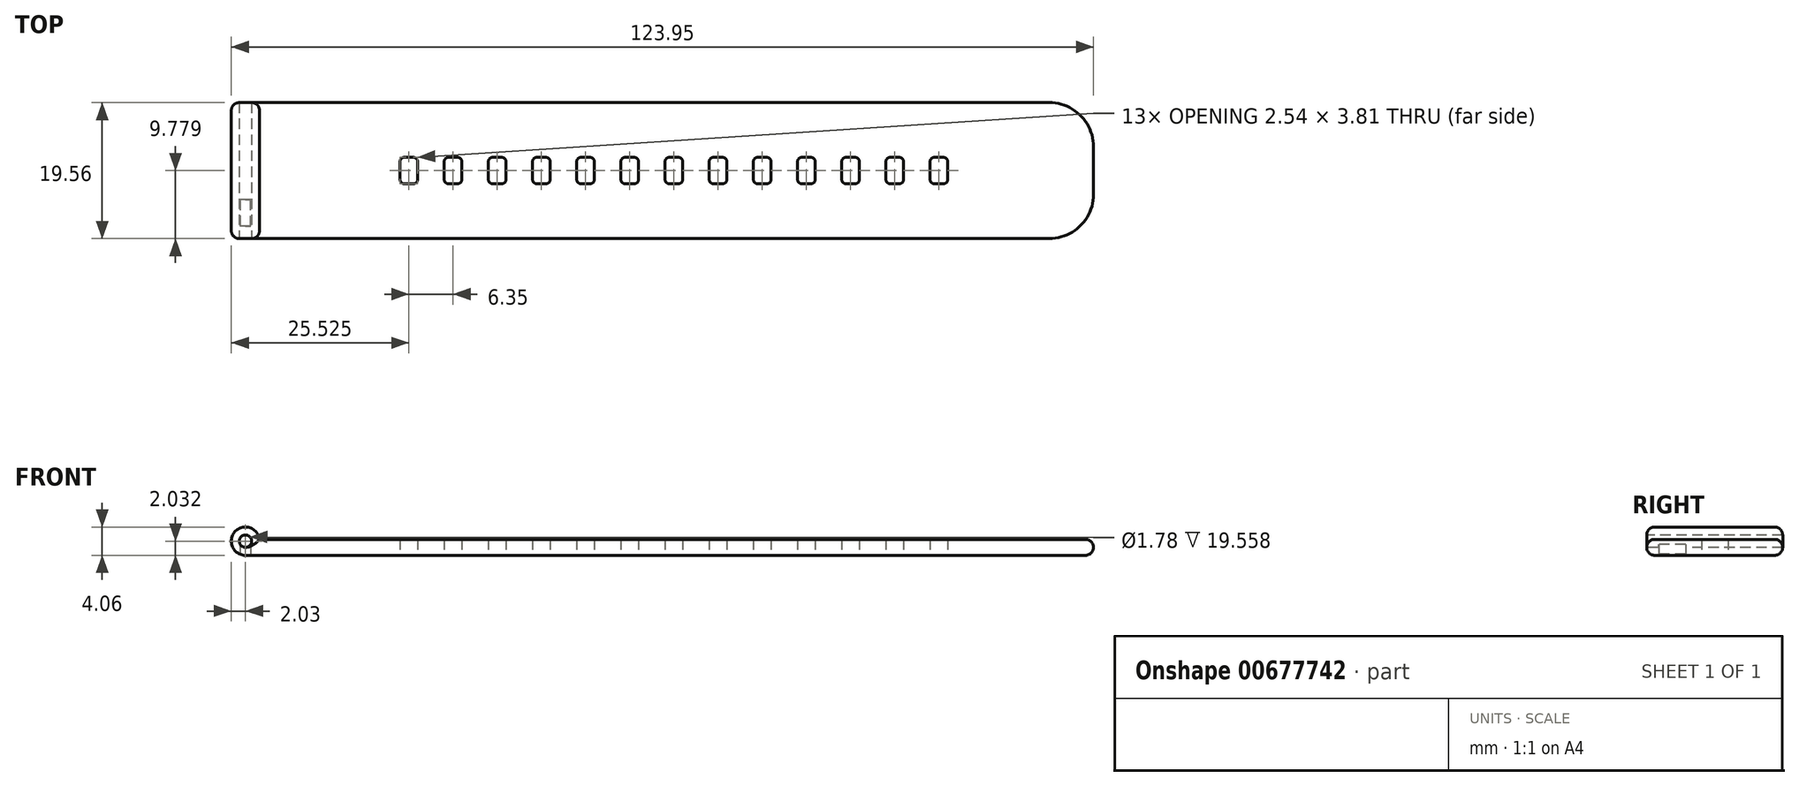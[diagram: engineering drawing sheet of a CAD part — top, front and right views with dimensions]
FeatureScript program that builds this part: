
annotation { "Feature Type Name" : "Feature", "Feature Type Description" : "" }
export const myFeature = defineFeature(function(context is Context, id is Id, definition is map)
    precondition{}
    {
        {
            var Q0;
            Q0=qCreatedBy(makeId("Top.planeOp"),FACE);
            var sketch = newSketch(context, id + "F0", { "sketchPlane" : qUnion([Q0])});
            skLineSegment(sketch, "E0.bottom", {"start": v(0, 0) * mm, "end": v(115.57, 0) * mm});
            skLineSegment(sketch, "E0.top", {"start": v(0, 19.56) * mm, "end": v(115.57, 19.56) * mm});
            skLineSegment(sketch, "E0.left", {"start": v(0, 0) * mm, "end": v(0, 19.56) * mm});
            skLineSegment(sketch, "E0.right", {"start": v(121.92, 6.35) * mm, "end": v(121.92, 13.2) * mm});
            skPoint(sketch, "E1.visualSharp", {"position": v(121.92, 19.56) * mm});
            skArc(sketch, "E1.filletArc", {"start": v(121.92, 13.2) * mm, "mid": v(120.06, 17.7) * mm, "end": v(115.57, 19.56) * mm});
            skPoint(sketch, "E2.visualSharp", {"position": v(121.92, 0) * mm});
            skArc(sketch, "E2.filletArc", {"start": v(115.57, 0) * mm, "mid": v(120.06, 1.86) * mm, "end": v(121.92, 6.35) * mm});
            skLineSegment(sketch, "E3.bottom", {"start": v(24.13, 7.87) * mm, "end": v(22.86, 7.87) * mm});
            skLineSegment(sketch, "E3.top", {"start": v(24.13, 11.68) * mm, "end": v(22.86, 11.68) * mm});
            skLineSegment(sketch, "E3.left", {"start": v(24.77, 8.5) * mm, "end": v(24.77, 11.05) * mm});
            skLineSegment(sketch, "E3.right", {"start": v(22.23, 8.5) * mm, "end": v(22.23, 11.05) * mm});
            skPoint(sketch, "E3.middle", {"position": v(23.5, 9.78) * mm});
            skPoint(sketch, "E3.middle.positionSnap0", {"position": v(0, 9.78) * mm});
            skPoint(sketch, "E3.centerSnap0", {"position": v(0, 9.78) * mm});
            skPoint(sketch, "E4.visualSharp", {"position": v(22.23, 11.68) * mm});
            skArc(sketch, "E4.filletArc", {"start": v(22.86, 11.68) * mm, "mid": v(22.41, 11.5) * mm, "end": v(22.22, 11.05) * mm});
            skPoint(sketch, "E5.visualSharp", {"position": v(24.77, 11.68) * mm});
            skArc(sketch, "E5.filletArc", {"start": v(24.77, 11.05) * mm, "mid": v(24.58, 11.5) * mm, "end": v(24.13, 11.68) * mm});
            skPoint(sketch, "E6.visualSharp", {"position": v(24.77, 7.87) * mm});
            skArc(sketch, "E6.filletArc", {"start": v(24.13, 7.87) * mm, "mid": v(24.58, 8.06) * mm, "end": v(24.77, 8.5) * mm});
            skPoint(sketch, "E7.visualSharp", {"position": v(22.23, 7.87) * mm});
            skArc(sketch, "E7.filletArc", {"start": v(22.23, 8.5) * mm, "mid": v(22.41, 8.06) * mm, "end": v(22.86, 7.87) * mm});
            skPoint(sketch, "E8.1.0.0", {"position": v(28.58, 7.87) * mm});
            skPoint(sketch, "E8.1.0.1", {"position": v(31.12, 7.87) * mm});
            skPoint(sketch, "E8.1.0.2", {"position": v(28.58, 11.68) * mm});
            skPoint(sketch, "E8.1.0.3", {"position": v(31.12, 11.68) * mm});
            skPoint(sketch, "E8.1.0.4", {"position": v(29.85, 9.78) * mm});
            skLineSegment(sketch, "E8.1.0.5", {"start": v(30.48, 11.68) * mm, "end": v(29.21, 11.68) * mm});
            skLineSegment(sketch, "E8.1.0.6", {"start": v(31.12, 8.5) * mm, "end": v(31.12, 11.05) * mm});
            skLineSegment(sketch, "E8.1.0.7", {"start": v(28.58, 8.5) * mm, "end": v(28.58, 11.05) * mm});
            skArc(sketch, "E8.1.0.8", {"start": v(31.12, 11.05) * mm, "mid": v(30.93, 11.5) * mm, "end": v(30.48, 11.68) * mm});
            skArc(sketch, "E8.1.0.9", {"start": v(29.21, 11.68) * mm, "mid": v(28.76, 11.5) * mm, "end": v(28.57, 11.05) * mm});
            skArc(sketch, "E8.1.0.10", {"start": v(30.48, 7.87) * mm, "mid": v(30.93, 8.06) * mm, "end": v(31.12, 8.5) * mm});
            skLineSegment(sketch, "E8.1.0.11", {"start": v(30.48, 7.87) * mm, "end": v(29.21, 7.87) * mm});
            skArc(sketch, "E8.1.0.12", {"start": v(28.58, 8.5) * mm, "mid": v(28.76, 8.06) * mm, "end": v(29.21, 7.87) * mm});
            skPoint(sketch, "E8.2.0.0", {"position": v(34.93, 7.87) * mm});
            skPoint(sketch, "E8.2.0.1", {"position": v(37.47, 7.87) * mm});
            skPoint(sketch, "E8.2.0.2", {"position": v(34.93, 11.68) * mm});
            skPoint(sketch, "E8.2.0.3", {"position": v(37.47, 11.68) * mm});
            skPoint(sketch, "E8.2.0.4", {"position": v(36.2, 9.78) * mm});
            skLineSegment(sketch, "E8.2.0.5", {"start": v(36.83, 11.68) * mm, "end": v(35.56, 11.68) * mm});
            skLineSegment(sketch, "E8.2.0.6", {"start": v(37.47, 8.5) * mm, "end": v(37.47, 11.05) * mm});
            skLineSegment(sketch, "E8.2.0.7", {"start": v(34.93, 8.5) * mm, "end": v(34.93, 11.05) * mm});
            skArc(sketch, "E8.2.0.8", {"start": v(37.46, 11.05) * mm, "mid": v(37.28, 11.5) * mm, "end": v(36.83, 11.68) * mm});
            skArc(sketch, "E8.2.0.9", {"start": v(35.56, 11.68) * mm, "mid": v(35.11, 11.5) * mm, "end": v(34.92, 11.05) * mm});
            skArc(sketch, "E8.2.0.10", {"start": v(36.83, 7.87) * mm, "mid": v(37.28, 8.06) * mm, "end": v(37.47, 8.5) * mm});
            skLineSegment(sketch, "E8.2.0.11", {"start": v(36.83, 7.87) * mm, "end": v(35.56, 7.87) * mm});
            skArc(sketch, "E8.2.0.12", {"start": v(34.93, 8.5) * mm, "mid": v(35.11, 8.06) * mm, "end": v(35.56, 7.87) * mm});
            skPoint(sketch, "E8.3.0.0", {"position": v(41.28, 7.87) * mm});
            skPoint(sketch, "E8.3.0.1", {"position": v(43.82, 7.87) * mm});
            skPoint(sketch, "E8.3.0.2", {"position": v(41.28, 11.68) * mm});
            skPoint(sketch, "E8.3.0.3", {"position": v(43.82, 11.68) * mm});
            skPoint(sketch, "E8.3.0.4", {"position": v(42.55, 9.78) * mm});
            skLineSegment(sketch, "E8.3.0.5", {"start": v(43.18, 11.68) * mm, "end": v(41.91, 11.68) * mm});
            skLineSegment(sketch, "E8.3.0.6", {"start": v(43.82, 8.5) * mm, "end": v(43.82, 11.05) * mm});
            skLineSegment(sketch, "E8.3.0.7", {"start": v(41.28, 8.5) * mm, "end": v(41.28, 11.05) * mm});
            skArc(sketch, "E8.3.0.8", {"start": v(43.82, 11.05) * mm, "mid": v(43.63, 11.5) * mm, "end": v(43.18, 11.68) * mm});
            skArc(sketch, "E8.3.0.9", {"start": v(41.91, 11.68) * mm, "mid": v(41.46, 11.5) * mm, "end": v(41.28, 11.05) * mm});
            skArc(sketch, "E8.3.0.10", {"start": v(43.18, 7.87) * mm, "mid": v(43.63, 8.06) * mm, "end": v(43.82, 8.5) * mm});
            skLineSegment(sketch, "E8.3.0.11", {"start": v(43.18, 7.87) * mm, "end": v(41.91, 7.87) * mm});
            skArc(sketch, "E8.3.0.12", {"start": v(41.28, 8.5) * mm, "mid": v(41.46, 8.06) * mm, "end": v(41.91, 7.87) * mm});
            skPoint(sketch, "E8.4.0.0", {"position": v(47.63, 7.87) * mm});
            skPoint(sketch, "E8.4.0.1", {"position": v(50.17, 7.87) * mm});
            skPoint(sketch, "E8.4.0.2", {"position": v(47.63, 11.68) * mm});
            skPoint(sketch, "E8.4.0.3", {"position": v(50.17, 11.68) * mm});
            skPoint(sketch, "E8.4.0.4", {"position": v(48.9, 9.78) * mm});
            skLineSegment(sketch, "E8.4.0.5", {"start": v(49.53, 11.68) * mm, "end": v(48.26, 11.68) * mm});
            skLineSegment(sketch, "E8.4.0.6", {"start": v(50.17, 8.5) * mm, "end": v(50.17, 11.05) * mm});
            skLineSegment(sketch, "E8.4.0.7", {"start": v(47.63, 8.5) * mm, "end": v(47.63, 11.05) * mm});
            skArc(sketch, "E8.4.0.8", {"start": v(50.16, 11.05) * mm, "mid": v(49.98, 11.5) * mm, "end": v(49.53, 11.68) * mm});
            skArc(sketch, "E8.4.0.9", {"start": v(48.26, 11.68) * mm, "mid": v(47.81, 11.5) * mm, "end": v(47.62, 11.05) * mm});
            skArc(sketch, "E8.4.0.10", {"start": v(49.53, 7.87) * mm, "mid": v(49.98, 8.06) * mm, "end": v(50.17, 8.5) * mm});
            skLineSegment(sketch, "E8.4.0.11", {"start": v(49.53, 7.87) * mm, "end": v(48.26, 7.87) * mm});
            skArc(sketch, "E8.4.0.12", {"start": v(47.63, 8.5) * mm, "mid": v(47.81, 8.06) * mm, "end": v(48.26, 7.87) * mm});
            skPoint(sketch, "E8.5.0.0", {"position": v(53.98, 7.87) * mm});
            skPoint(sketch, "E8.5.0.1", {"position": v(56.52, 7.87) * mm});
            skPoint(sketch, "E8.5.0.2", {"position": v(53.98, 11.68) * mm});
            skPoint(sketch, "E8.5.0.3", {"position": v(56.52, 11.68) * mm});
            skPoint(sketch, "E8.5.0.4", {"position": v(55.25, 9.78) * mm});
            skLineSegment(sketch, "E8.5.0.5", {"start": v(55.88, 11.68) * mm, "end": v(54.61, 11.68) * mm});
            skLineSegment(sketch, "E8.5.0.6", {"start": v(56.52, 8.5) * mm, "end": v(56.52, 11.05) * mm});
            skLineSegment(sketch, "E8.5.0.7", {"start": v(53.98, 8.5) * mm, "end": v(53.98, 11.05) * mm});
            skArc(sketch, "E8.5.0.8", {"start": v(56.52, 11.05) * mm, "mid": v(56.33, 11.5) * mm, "end": v(55.88, 11.68) * mm});
            skArc(sketch, "E8.5.0.9", {"start": v(54.61, 11.68) * mm, "mid": v(54.16, 11.5) * mm, "end": v(53.98, 11.05) * mm});
            skArc(sketch, "E8.5.0.10", {"start": v(55.88, 7.87) * mm, "mid": v(56.33, 8.06) * mm, "end": v(56.52, 8.5) * mm});
            skLineSegment(sketch, "E8.5.0.11", {"start": v(55.88, 7.87) * mm, "end": v(54.61, 7.87) * mm});
            skArc(sketch, "E8.5.0.12", {"start": v(53.98, 8.5) * mm, "mid": v(54.16, 8.06) * mm, "end": v(54.61, 7.87) * mm});
            skPoint(sketch, "E8.6.0.0", {"position": v(60.33, 7.87) * mm});
            skPoint(sketch, "E8.6.0.1", {"position": v(62.87, 7.87) * mm});
            skPoint(sketch, "E8.6.0.2", {"position": v(60.33, 11.68) * mm});
            skPoint(sketch, "E8.6.0.3", {"position": v(62.87, 11.68) * mm});
            skPoint(sketch, "E8.6.0.4", {"position": v(61.6, 9.78) * mm});
            skLineSegment(sketch, "E8.6.0.5", {"start": v(62.23, 11.68) * mm, "end": v(60.96, 11.68) * mm});
            skLineSegment(sketch, "E8.6.0.6", {"start": v(62.87, 8.5) * mm, "end": v(62.87, 11.05) * mm});
            skLineSegment(sketch, "E8.6.0.7", {"start": v(60.33, 8.5) * mm, "end": v(60.33, 11.05) * mm});
            skArc(sketch, "E8.6.0.8", {"start": v(62.87, 11.05) * mm, "mid": v(62.68, 11.5) * mm, "end": v(62.23, 11.68) * mm});
            skArc(sketch, "E8.6.0.9", {"start": v(60.96, 11.68) * mm, "mid": v(60.51, 11.5) * mm, "end": v(60.33, 11.05) * mm});
            skArc(sketch, "E8.6.0.10", {"start": v(62.23, 7.87) * mm, "mid": v(62.68, 8.06) * mm, "end": v(62.87, 8.5) * mm});
            skLineSegment(sketch, "E8.6.0.11", {"start": v(62.23, 7.87) * mm, "end": v(60.96, 7.87) * mm});
            skArc(sketch, "E8.6.0.12", {"start": v(60.33, 8.5) * mm, "mid": v(60.51, 8.06) * mm, "end": v(60.96, 7.87) * mm});
            skPoint(sketch, "E8.7.0.0", {"position": v(66.68, 7.87) * mm});
            skPoint(sketch, "E8.7.0.1", {"position": v(69.22, 7.87) * mm});
            skPoint(sketch, "E8.7.0.2", {"position": v(66.68, 11.68) * mm});
            skPoint(sketch, "E8.7.0.3", {"position": v(69.22, 11.68) * mm});
            skPoint(sketch, "E8.7.0.4", {"position": v(67.95, 9.78) * mm});
            skLineSegment(sketch, "E8.7.0.5", {"start": v(68.58, 11.68) * mm, "end": v(67.31, 11.68) * mm});
            skLineSegment(sketch, "E8.7.0.6", {"start": v(69.22, 8.5) * mm, "end": v(69.22, 11.05) * mm});
            skLineSegment(sketch, "E8.7.0.7", {"start": v(66.68, 8.5) * mm, "end": v(66.68, 11.05) * mm});
            skArc(sketch, "E8.7.0.8", {"start": v(69.22, 11.05) * mm, "mid": v(69.03, 11.5) * mm, "end": v(68.58, 11.68) * mm});
            skArc(sketch, "E8.7.0.9", {"start": v(67.31, 11.68) * mm, "mid": v(66.86, 11.5) * mm, "end": v(66.68, 11.05) * mm});
            skArc(sketch, "E8.7.0.10", {"start": v(68.58, 7.87) * mm, "mid": v(69.03, 8.06) * mm, "end": v(69.22, 8.5) * mm});
            skLineSegment(sketch, "E8.7.0.11", {"start": v(68.58, 7.87) * mm, "end": v(67.31, 7.87) * mm});
            skArc(sketch, "E8.7.0.12", {"start": v(66.68, 8.5) * mm, "mid": v(66.86, 8.06) * mm, "end": v(67.31, 7.87) * mm});
            skPoint(sketch, "E8.8.0.0", {"position": v(73.03, 7.87) * mm});
            skPoint(sketch, "E8.8.0.1", {"position": v(75.57, 7.87) * mm});
            skPoint(sketch, "E8.8.0.2", {"position": v(73.03, 11.68) * mm});
            skPoint(sketch, "E8.8.0.3", {"position": v(75.57, 11.68) * mm});
            skPoint(sketch, "E8.8.0.4", {"position": v(74.3, 9.78) * mm});
            skLineSegment(sketch, "E8.8.0.5", {"start": v(74.93, 11.68) * mm, "end": v(73.66, 11.68) * mm});
            skLineSegment(sketch, "E8.8.0.6", {"start": v(75.57, 8.5) * mm, "end": v(75.57, 11.05) * mm});
            skLineSegment(sketch, "E8.8.0.7", {"start": v(73.03, 8.5) * mm, "end": v(73.03, 11.05) * mm});
            skArc(sketch, "E8.8.0.8", {"start": v(75.57, 11.05) * mm, "mid": v(75.38, 11.5) * mm, "end": v(74.93, 11.68) * mm});
            skArc(sketch, "E8.8.0.9", {"start": v(73.66, 11.68) * mm, "mid": v(73.21, 11.5) * mm, "end": v(73.03, 11.05) * mm});
            skArc(sketch, "E8.8.0.10", {"start": v(74.93, 7.87) * mm, "mid": v(75.38, 8.06) * mm, "end": v(75.57, 8.5) * mm});
            skLineSegment(sketch, "E8.8.0.11", {"start": v(74.93, 7.87) * mm, "end": v(73.66, 7.87) * mm});
            skArc(sketch, "E8.8.0.12", {"start": v(73.03, 8.5) * mm, "mid": v(73.21, 8.06) * mm, "end": v(73.66, 7.87) * mm});
            skPoint(sketch, "E8.9.0.0", {"position": v(79.38, 7.87) * mm});
            skPoint(sketch, "E8.9.0.1", {"position": v(81.92, 7.87) * mm});
            skPoint(sketch, "E8.9.0.2", {"position": v(79.38, 11.68) * mm});
            skPoint(sketch, "E8.9.0.3", {"position": v(81.92, 11.68) * mm});
            skPoint(sketch, "E8.9.0.4", {"position": v(80.65, 9.78) * mm});
            skLineSegment(sketch, "E8.9.0.5", {"start": v(81.28, 11.68) * mm, "end": v(80.01, 11.68) * mm});
            skLineSegment(sketch, "E8.9.0.6", {"start": v(81.92, 8.5) * mm, "end": v(81.92, 11.05) * mm});
            skLineSegment(sketch, "E8.9.0.7", {"start": v(79.38, 8.5) * mm, "end": v(79.38, 11.05) * mm});
            skArc(sketch, "E8.9.0.8", {"start": v(81.92, 11.05) * mm, "mid": v(81.73, 11.5) * mm, "end": v(81.28, 11.68) * mm});
            skArc(sketch, "E8.9.0.9", {"start": v(80.01, 11.68) * mm, "mid": v(79.56, 11.5) * mm, "end": v(79.38, 11.05) * mm});
            skArc(sketch, "E8.9.0.10", {"start": v(81.28, 7.87) * mm, "mid": v(81.73, 8.06) * mm, "end": v(81.92, 8.5) * mm});
            skLineSegment(sketch, "E8.9.0.11", {"start": v(81.28, 7.87) * mm, "end": v(80.01, 7.87) * mm});
            skArc(sketch, "E8.9.0.12", {"start": v(79.38, 8.5) * mm, "mid": v(79.56, 8.06) * mm, "end": v(80.01, 7.87) * mm});
            skPoint(sketch, "E8.10.0.0", {"position": v(85.73, 7.87) * mm});
            skPoint(sketch, "E8.10.0.1", {"position": v(88.27, 7.87) * mm});
            skPoint(sketch, "E8.10.0.2", {"position": v(85.73, 11.68) * mm});
            skPoint(sketch, "E8.10.0.3", {"position": v(88.27, 11.68) * mm});
            skPoint(sketch, "E8.10.0.4", {"position": v(87, 9.78) * mm});
            skLineSegment(sketch, "E8.10.0.5", {"start": v(87.63, 11.68) * mm, "end": v(86.36, 11.68) * mm});
            skLineSegment(sketch, "E8.10.0.6", {"start": v(88.27, 8.5) * mm, "end": v(88.27, 11.05) * mm});
            skLineSegment(sketch, "E8.10.0.7", {"start": v(85.73, 8.5) * mm, "end": v(85.73, 11.05) * mm});
            skArc(sketch, "E8.10.0.8", {"start": v(88.27, 11.05) * mm, "mid": v(88.08, 11.5) * mm, "end": v(87.63, 11.68) * mm});
            skArc(sketch, "E8.10.0.9", {"start": v(86.36, 11.68) * mm, "mid": v(85.91, 11.5) * mm, "end": v(85.73, 11.05) * mm});
            skArc(sketch, "E8.10.0.10", {"start": v(87.63, 7.87) * mm, "mid": v(88.08, 8.06) * mm, "end": v(88.27, 8.5) * mm});
            skLineSegment(sketch, "E8.10.0.11", {"start": v(87.63, 7.87) * mm, "end": v(86.36, 7.87) * mm});
            skArc(sketch, "E8.10.0.12", {"start": v(85.73, 8.5) * mm, "mid": v(85.91, 8.06) * mm, "end": v(86.36, 7.87) * mm});
            skPoint(sketch, "E8.11.0.0", {"position": v(92.08, 7.87) * mm});
            skPoint(sketch, "E8.11.0.1", {"position": v(94.62, 7.87) * mm});
            skPoint(sketch, "E8.11.0.2", {"position": v(92.08, 11.68) * mm});
            skPoint(sketch, "E8.11.0.3", {"position": v(94.62, 11.68) * mm});
            skPoint(sketch, "E8.11.0.4", {"position": v(93.35, 9.78) * mm});
            skLineSegment(sketch, "E8.11.0.5", {"start": v(93.98, 11.68) * mm, "end": v(92.71, 11.68) * mm});
            skLineSegment(sketch, "E8.11.0.6", {"start": v(94.62, 8.5) * mm, "end": v(94.62, 11.05) * mm});
            skLineSegment(sketch, "E8.11.0.7", {"start": v(92.08, 8.5) * mm, "end": v(92.08, 11.05) * mm});
            skArc(sketch, "E8.11.0.8", {"start": v(94.62, 11.05) * mm, "mid": v(94.43, 11.5) * mm, "end": v(93.98, 11.68) * mm});
            skArc(sketch, "E8.11.0.9", {"start": v(92.71, 11.68) * mm, "mid": v(92.26, 11.5) * mm, "end": v(92.08, 11.05) * mm});
            skArc(sketch, "E8.11.0.10", {"start": v(93.98, 7.87) * mm, "mid": v(94.43, 8.06) * mm, "end": v(94.62, 8.5) * mm});
            skLineSegment(sketch, "E8.11.0.11", {"start": v(93.98, 7.87) * mm, "end": v(92.71, 7.87) * mm});
            skArc(sketch, "E8.11.0.12", {"start": v(92.08, 8.5) * mm, "mid": v(92.26, 8.06) * mm, "end": v(92.71, 7.87) * mm});
            skPoint(sketch, "E8.12.0.0", {"position": v(98.43, 7.87) * mm});
            skPoint(sketch, "E8.12.0.1", {"position": v(100.97, 7.87) * mm});
            skPoint(sketch, "E8.12.0.2", {"position": v(98.43, 11.68) * mm});
            skPoint(sketch, "E8.12.0.3", {"position": v(100.97, 11.68) * mm});
            skPoint(sketch, "E8.12.0.4", {"position": v(99.7, 9.78) * mm});
            skLineSegment(sketch, "E8.12.0.5", {"start": v(100.33, 11.68) * mm, "end": v(99.06, 11.68) * mm});
            skLineSegment(sketch, "E8.12.0.6", {"start": v(100.97, 8.5) * mm, "end": v(100.97, 11.05) * mm});
            skLineSegment(sketch, "E8.12.0.7", {"start": v(98.43, 8.5) * mm, "end": v(98.43, 11.05) * mm});
            skArc(sketch, "E8.12.0.8", {"start": v(100.97, 11.05) * mm, "mid": v(100.78, 11.5) * mm, "end": v(100.33, 11.68) * mm});
            skArc(sketch, "E8.12.0.9", {"start": v(99.06, 11.68) * mm, "mid": v(98.61, 11.5) * mm, "end": v(98.43, 11.05) * mm});
            skArc(sketch, "E8.12.0.10", {"start": v(100.33, 7.87) * mm, "mid": v(100.78, 8.06) * mm, "end": v(100.97, 8.5) * mm});
            skLineSegment(sketch, "E8.12.0.11", {"start": v(100.33, 7.87) * mm, "end": v(99.06, 7.87) * mm});
            skArc(sketch, "E8.12.0.12", {"start": v(98.43, 8.5) * mm, "mid": v(98.61, 8.06) * mm, "end": v(99.06, 7.87) * mm});
            skLineSegment(sketch, "E8.direction1", {"start": v(22.23, 7.87) * mm, "end": v(28.58, 7.87) * mm, "construction": true});
            skSolve(sketch);
        }
        {
            var Q0;
            Q0=makeQuery(id+"F0.imprint","IMPRINT",FACE,{"disambiguationData":[TD([[makeQuery(id+"F0.imprint","IMPRINT",EDGE,{"derivedFrom":sQuery(id+"F0.wireOp",EDGE,"E0.bottom")}),1.0]])]});
            extrude(context, id + "F1", {"entities" : qUnion([Q0]), "depth" : 2.3 * mm, "offsetDistance" : 25.4 * mm});
        }
        {
            var Q0;
            Q0=makeQuery(id+"F1.opExtrude","SWEPT_FACE",FACE,{"disambiguationData":[OSD([sQuery(id+"F0.wireOp",EDGE,"E0.bottom")])]});
            var sketch = newSketch(context, id + "F2", { "sketchPlane" : qUnion([Q0])});
            skCircle(sketch, "E9", {"center": v(0, 2.03) * mm, "radius": 0.89 * mm});
            skCircle(sketch, "E10.0", {"center": v(0, 2.03) * mm, "radius": 2.03 * mm});
            skSolve(sketch);
        }
        {
            var Q0;
            {var subQ0=sQuery(id+"F2.wireOp",EDGE,"E9");var subQ1=makeQuery(id+"F1.opExtrude","SWEPT_EDGE",EDGE,{"disambiguationData":[OSD([sQuery(id+"F0.wireOp",EDGE,"E0.bottom"),sQuery(id+"F0.wireOp",EDGE,"E0.left")])]});var subQ2=makeQuery(id+"F2.imprint","INTERSECT",VERTEX,{"disambiguationData":[OD(0.0)],"derivedFrom":[subQ1,subQ0]});Q0=makeQuery(id+"F2.imprint","IMPRINT",FACE,{"disambiguationData":[TD([[makeQuery(id+"F2.imprint","IMPRINT",EDGE,{"disambiguationData":[TD([[subQ2,-1.0]])],"derivedFrom":subQ0}),1.0]])]});}
            extrude(context, id + "F3", {"entities" : qUnion([Q0]), "operationType" : NewBodyOperationType.REMOVE, "endBound" : BoundingType.THROUGH_ALL, "oppositeDirection" : true, "depth" : 25.4 * mm, "offsetDistance" : 25.4 * mm});
        }
        {
            var Q0;
            {var subQ0=sQuery(id+"F0.wireOp",EDGE,"E0.bottom");var subQ6=sQuery(id+"F2.wireOp",EDGE,"E10.0");var subQ7=makeQuery(id+"F1.opExtrude","CAP_EDGE",EDGE,{"disambiguationData":[OSD([subQ0])],"isStart":true});var subQ8=makeQuery(id+"F2.imprint","INTERSECT",VERTEX,{"derivedFrom":[subQ7,subQ6]});Q0=makeQuery(id+"F2.imprint","IMPRINT",FACE,{"disambiguationData":[TD([[makeQuery(id+"F2.imprint","IMPRINT",EDGE,{"disambiguationData":[TD([[subQ8,1.0]])],"derivedFrom":subQ6}),1.0]])]});}
            var Q1;
            Q1=makeQuery(id+"F1.opExtrude","SWEPT_FACE",FACE,{"disambiguationData":[OSD([sQuery(id+"F0.wireOp",EDGE,"E0.top")])]});
            extrude(context, id + "F4", {"entities" : qUnion([Q0]), "operationType" : NewBodyOperationType.ADD, "endBound" : BoundingType.UP_TO_SURFACE, "oppositeDirection" : true, "depth" : 25.4 * mm, "endBoundEntityFace" : qUnion([Q1]), "offsetDistance" : 25.4 * mm});
        }
        {
            var Q0;
            Q0=makeQuery(id+"F1.opExtrude","CAP_FACE",FACE,{"disambiguationData":[OSD([sQuery(id+"F0.wireOp",EDGE,"E0.bottom"),sQuery(id+"F0.wireOp",EDGE,"E0.top"),sQuery(id+"F0.wireOp",EDGE,"E0.left"),sQuery(id+"F0.wireOp",EDGE,"E0.right"),sQuery(id+"F0.wireOp",EDGE,"E1.filletArc"),sQuery(id+"F0.wireOp",EDGE,"E2.filletArc"),sQuery(id+"F0.wireOp",EDGE,"E3.bottom"),sQuery(id+"F0.wireOp",EDGE,"E3.top"),sQuery(id+"F0.wireOp",EDGE,"E3.left"),sQuery(id+"F0.wireOp",EDGE,"E3.right"),sQuery(id+"F0.wireOp",EDGE,"E4.filletArc"),sQuery(id+"F0.wireOp",EDGE,"E5.filletArc"),sQuery(id+"F0.wireOp",EDGE,"E6.filletArc"),sQuery(id+"F0.wireOp",EDGE,"E7.filletArc"),sQuery(id+"F0.wireOp",EDGE,"E8.1.0.5"),sQuery(id+"F0.wireOp",EDGE,"E8.1.0.6"),sQuery(id+"F0.wireOp",EDGE,"E8.1.0.7"),sQuery(id+"F0.wireOp",EDGE,"E8.1.0.8"),sQuery(id+"F0.wireOp",EDGE,"E8.1.0.9"),sQuery(id+"F0.wireOp",EDGE,"E8.1.0.10"),sQuery(id+"F0.wireOp",EDGE,"E8.1.0.11"),sQuery(id+"F0.wireOp",EDGE,"E8.1.0.12"),sQuery(id+"F0.wireOp",EDGE,"E8.2.0.5"),sQuery(id+"F0.wireOp",EDGE,"E8.2.0.6"),sQuery(id+"F0.wireOp",EDGE,"E8.2.0.7"),sQuery(id+"F0.wireOp",EDGE,"E8.2.0.8"),sQuery(id+"F0.wireOp",EDGE,"E8.2.0.9"),sQuery(id+"F0.wireOp",EDGE,"E8.2.0.10"),sQuery(id+"F0.wireOp",EDGE,"E8.2.0.11"),sQuery(id+"F0.wireOp",EDGE,"E8.2.0.12"),sQuery(id+"F0.wireOp",EDGE,"E8.3.0.5"),sQuery(id+"F0.wireOp",EDGE,"E8.3.0.6"),sQuery(id+"F0.wireOp",EDGE,"E8.3.0.7"),sQuery(id+"F0.wireOp",EDGE,"E8.3.0.8"),sQuery(id+"F0.wireOp",EDGE,"E8.3.0.9"),sQuery(id+"F0.wireOp",EDGE,"E8.3.0.10"),sQuery(id+"F0.wireOp",EDGE,"E8.3.0.11"),sQuery(id+"F0.wireOp",EDGE,"E8.3.0.12"),sQuery(id+"F0.wireOp",EDGE,"E8.4.0.5"),sQuery(id+"F0.wireOp",EDGE,"E8.4.0.6"),sQuery(id+"F0.wireOp",EDGE,"E8.4.0.7"),sQuery(id+"F0.wireOp",EDGE,"E8.4.0.8"),sQuery(id+"F0.wireOp",EDGE,"E8.4.0.9"),sQuery(id+"F0.wireOp",EDGE,"E8.4.0.10"),sQuery(id+"F0.wireOp",EDGE,"E8.4.0.11"),sQuery(id+"F0.wireOp",EDGE,"E8.4.0.12"),sQuery(id+"F0.wireOp",EDGE,"E8.5.0.5"),sQuery(id+"F0.wireOp",EDGE,"E8.5.0.6"),sQuery(id+"F0.wireOp",EDGE,"E8.5.0.7"),sQuery(id+"F0.wireOp",EDGE,"E8.5.0.8"),sQuery(id+"F0.wireOp",EDGE,"E8.5.0.9"),sQuery(id+"F0.wireOp",EDGE,"E8.5.0.10"),sQuery(id+"F0.wireOp",EDGE,"E8.5.0.11"),sQuery(id+"F0.wireOp",EDGE,"E8.5.0.12"),sQuery(id+"F0.wireOp",EDGE,"E8.6.0.5"),sQuery(id+"F0.wireOp",EDGE,"E8.6.0.6"),sQuery(id+"F0.wireOp",EDGE,"E8.6.0.7"),sQuery(id+"F0.wireOp",EDGE,"E8.6.0.8"),sQuery(id+"F0.wireOp",EDGE,"E8.6.0.9"),sQuery(id+"F0.wireOp",EDGE,"E8.6.0.10"),sQuery(id+"F0.wireOp",EDGE,"E8.6.0.11"),sQuery(id+"F0.wireOp",EDGE,"E8.6.0.12"),sQuery(id+"F0.wireOp",EDGE,"E8.7.0.5"),sQuery(id+"F0.wireOp",EDGE,"E8.7.0.6"),sQuery(id+"F0.wireOp",EDGE,"E8.7.0.7"),sQuery(id+"F0.wireOp",EDGE,"E8.7.0.8"),sQuery(id+"F0.wireOp",EDGE,"E8.7.0.9"),sQuery(id+"F0.wireOp",EDGE,"E8.7.0.10"),sQuery(id+"F0.wireOp",EDGE,"E8.7.0.11"),sQuery(id+"F0.wireOp",EDGE,"E8.7.0.12"),sQuery(id+"F0.wireOp",EDGE,"E8.8.0.5"),sQuery(id+"F0.wireOp",EDGE,"E8.8.0.6"),sQuery(id+"F0.wireOp",EDGE,"E8.8.0.7"),sQuery(id+"F0.wireOp",EDGE,"E8.8.0.8"),sQuery(id+"F0.wireOp",EDGE,"E8.8.0.9"),sQuery(id+"F0.wireOp",EDGE,"E8.8.0.10"),sQuery(id+"F0.wireOp",EDGE,"E8.8.0.11"),sQuery(id+"F0.wireOp",EDGE,"E8.8.0.12"),sQuery(id+"F0.wireOp",EDGE,"E8.9.0.5"),sQuery(id+"F0.wireOp",EDGE,"E8.9.0.6"),sQuery(id+"F0.wireOp",EDGE,"E8.9.0.7"),sQuery(id+"F0.wireOp",EDGE,"E8.9.0.8"),sQuery(id+"F0.wireOp",EDGE,"E8.9.0.9"),sQuery(id+"F0.wireOp",EDGE,"E8.9.0.10"),sQuery(id+"F0.wireOp",EDGE,"E8.9.0.11"),sQuery(id+"F0.wireOp",EDGE,"E8.9.0.12"),sQuery(id+"F0.wireOp",EDGE,"E8.10.0.5"),sQuery(id+"F0.wireOp",EDGE,"E8.10.0.6"),sQuery(id+"F0.wireOp",EDGE,"E8.10.0.7"),sQuery(id+"F0.wireOp",EDGE,"E8.10.0.8"),sQuery(id+"F0.wireOp",EDGE,"E8.10.0.9"),sQuery(id+"F0.wireOp",EDGE,"E8.10.0.10"),sQuery(id+"F0.wireOp",EDGE,"E8.10.0.11"),sQuery(id+"F0.wireOp",EDGE,"E8.10.0.12"),sQuery(id+"F0.wireOp",EDGE,"E8.11.0.5"),sQuery(id+"F0.wireOp",EDGE,"E8.11.0.6"),sQuery(id+"F0.wireOp",EDGE,"E8.11.0.7"),sQuery(id+"F0.wireOp",EDGE,"E8.11.0.8"),sQuery(id+"F0.wireOp",EDGE,"E8.11.0.9"),sQuery(id+"F0.wireOp",EDGE,"E8.11.0.10"),sQuery(id+"F0.wireOp",EDGE,"E8.11.0.11"),sQuery(id+"F0.wireOp",EDGE,"E8.11.0.12"),sQuery(id+"F0.wireOp",EDGE,"E8.12.0.5"),sQuery(id+"F0.wireOp",EDGE,"E8.12.0.6"),sQuery(id+"F0.wireOp",EDGE,"E8.12.0.7"),sQuery(id+"F0.wireOp",EDGE,"E8.12.0.8"),sQuery(id+"F0.wireOp",EDGE,"E8.12.0.9"),sQuery(id+"F0.wireOp",EDGE,"E8.12.0.10"),sQuery(id+"F0.wireOp",EDGE,"E8.12.0.11"),sQuery(id+"F0.wireOp",EDGE,"E8.12.0.12")])],"isStart":true});
            var sketch = newSketch(context, id + "F5", { "sketchPlane" : qUnion([Q0])});
            skLineSegment(sketch, "E11.bottom", {"start": v(-0.76, -1.78) * mm, "end": v(0.76, -1.78) * mm});
            skLineSegment(sketch, "E11.top", {"start": v(-0.76, -5.59) * mm, "end": v(0.76, -5.59) * mm});
            skLineSegment(sketch, "E11.left", {"start": v(-0.76, -1.78) * mm, "end": v(-0.76, -5.59) * mm});
            skLineSegment(sketch, "E11.right", {"start": v(0.76, -1.78) * mm, "end": v(0.76, -5.59) * mm});
            skPoint(sketch, "E11.middle", {"position": v(0, -3.68) * mm});
            skSolve(sketch);
        }
        {
            var Q0;
            {var subQ0=sQuery(id+"F5.wireOp",EDGE,"E11.left");Q0=makeQuery(id+"F5.imprint","IMPRINT",FACE,{"disambiguationData":[TD([[makeQuery(id+"F5.imprint","IMPRINT",EDGE,{"derivedFrom":subQ0}),1.0]])]});}
            var Q1;
            {var subQ0=sQuery(id+"F5.wireOp",EDGE,"E11.right");Q1=makeQuery(id+"F5.imprint","IMPRINT",FACE,{"disambiguationData":[TD([[makeQuery(id+"F5.imprint","IMPRINT",EDGE,{"derivedFrom":subQ0}),-1.0]])]});}
            extrude(context, id + "F6", {"entities" : qUnion([Q0, Q1]), "operationType" : NewBodyOperationType.REMOVE, "endBound" : BoundingType.UP_TO_NEXT, "oppositeDirection" : true, "depth" : 25.4 * mm, "offsetDistance" : 25.4 * mm});
        }
        {
            var Q0;
            Q0=qCreatedBy(makeId("Top.planeOp"),FACE);
            var sketch = newSketch(context, id + "F7", { "sketchPlane" : qUnion([Q0])});
            skLineSegment(sketch, "E12.bottom", {"start": v(0, 25.9) * mm, "end": v(76.2, 25.9) * mm});
            skLineSegment(sketch, "E12.top", {"start": v(0, 45.47) * mm, "end": v(76.2, 45.47) * mm});
            skLineSegment(sketch, "E12.left", {"start": v(0, 25.9) * mm, "end": v(0, 45.47) * mm});
            skLineSegment(sketch, "E12.right", {"start": v(76.2, 25.9) * mm, "end": v(76.2, 45.47) * mm});
            skSolve(sketch);
        }
        {
            var Q0;
            Q0=makeQuery(id+"F7.imprint","IMPRINT",FACE,{"disambiguationData":[TD([[makeQuery(id+"F7.imprint","IMPRINT",EDGE,{"derivedFrom":sQuery(id+"F7.wireOp",EDGE,"E12.bottom")}),1.0]])]});
            extrude(context, id + "F8", {"entities" : qUnion([Q0]), "depth" : 2.3 * mm, "offsetDistance" : 25.4 * mm});
        }
        {
            var Q0;
            Q0=makeQuery(id+"F8.opExtrude","SWEPT_FACE",FACE,{"disambiguationData":[OSD([sQuery(id+"F7.wireOp",EDGE,"E12.bottom")])]});
            var sketch = newSketch(context, id + "F9", { "sketchPlane" : qUnion([Q0])});
            skCircle(sketch, "E13", {"center": v(0, 2.03) * mm, "radius": 2.03 * mm});
            skCircle(sketch, "E14", {"center": v(0, 2.03) * mm, "radius": 0.89 * mm});
            skSolve(sketch);
        }
        {
            var Q0;
            {var subQ0=sQuery(id+"F9.wireOp",EDGE,"E14");var subQ1=sQuery(id+"F7.wireOp",EDGE,"E12.bottom");var subQ4=makeQuery(id+"F8.opExtrude","CAP_EDGE",EDGE,{"disambiguationData":[OSD([subQ1])],"isStart":false});var subQ5=makeQuery(id+"F9.imprint","INTERSECT",VERTEX,{"derivedFrom":[subQ4,subQ0]});Q0=makeQuery(id+"F9.imprint","IMPRINT",FACE,{"disambiguationData":[TD([[makeQuery(id+"F9.imprint","IMPRINT",EDGE,{"disambiguationData":[TD([[subQ5,1.0]])],"derivedFrom":subQ0}),1.0]])]});}
            extrude(context, id + "F10", {"entities" : qUnion([Q0]), "operationType" : NewBodyOperationType.REMOVE, "endBound" : BoundingType.THROUGH_ALL, "oppositeDirection" : true, "depth" : 25.4 * mm, "offsetDistance" : 25.4 * mm});
        }
        {
            var Q0;
            Q0=qSketchRegion(id+"F9",true);
            var Q1;
            Q1=makeQuery(id+"F8.opExtrude","SWEPT_FACE",FACE,{"disambiguationData":[OSD([sQuery(id+"F7.wireOp",EDGE,"E12.top")])]});
            extrude(context, id + "F11", {"entities" : qUnion([Q0]), "operationType" : NewBodyOperationType.ADD, "endBound" : BoundingType.UP_TO_SURFACE, "oppositeDirection" : true, "depth" : 25.4 * mm, "endBoundEntityFace" : qUnion([Q1]), "offsetDistance" : 25.4 * mm});
        }
        {
            var Q0;
            Q0=makeQuery(id+"F11.boolean.opBoolean","MERGE",FACE,{"derivedFrom":[makeQuery(id+"F8.opExtrude","SWEPT_FACE",FACE,{"disambiguationData":[OSD([sQuery(id+"F7.wireOp",EDGE,"E12.bottom")])]}),makeQuery(id+"F11.opExtrude","CAP_FACE",FACE,{"disambiguationData":[OSD([sQuery(id+"F9.wireOp",EDGE,"E13"),sQuery(id+"F9.wireOp",EDGE,"E14")])],"isStart":true})]});
            var sketch = newSketch(context, id + "F12", { "sketchPlane" : qUnion([Q0])});
            skCircle(sketch, "E15", {"center": v(78.36, 2.03) * mm, "radius": 2.03 * mm});
            skCircle(sketch, "E16", {"center": v(78.36, 2.03) * mm, "radius": 0.89 * mm});
            skLineSegment(sketch, "E17", {"start": v(78.36, 0) * mm, "end": v(76.2, 0) * mm});
            skLineSegment(sketch, "E18", {"start": v(76.2, 2.29) * mm, "end": v(76.34, 2.29) * mm});
            skSolve(sketch);
        }
        {
            var Q0;
            Q0=makeQuery(id+"F12.imprint","IMPRINT",FACE,{"disambiguationData":[TD([[makeQuery(id+"F12.imprint","IMPRINT",EDGE,{"derivedFrom":sQuery(id+"F12.wireOp",EDGE,"E16")}),-1.0]])]});
            var Q1;
            {var subQ0=sQuery(id+"F12.wireOp",EDGE,"E17");Q1=makeQuery(id+"F12.imprint","IMPRINT",FACE,{"disambiguationData":[TD([[makeQuery(id+"F12.imprint","IMPRINT",EDGE,{"derivedFrom":subQ0}),-1.0]])]});}
            extrude(context, id + "F13", {"entities" : qUnion([Q0, Q1]), "operationType" : NewBodyOperationType.ADD, "oppositeDirection" : true, "depth" : 7.62 * mm, "offsetDistance" : 25.4 * mm});
        }
        {
            var Q0;
            {var subQ0=sQuery(id+"F7.wireOp",EDGE,"E12.top");Q0=makeQuery(id+"F11.boolean.opBoolean","MERGE",FACE,{"derivedFrom":[makeQuery(id+"F8.opExtrude","SWEPT_FACE",FACE,{"disambiguationData":[OSD([subQ0])]}),makeQuery(id+"F11.opExtrude","CAP_FACE",FACE,{"disambiguationData":[OSD([subQ0])],"isStart":false})]});}
            var sketch = newSketch(context, id + "F14", { "sketchPlane" : qUnion([Q0])});
            skCircle(sketch, "E19.0", {"center": v(-78.36, 2.03) * mm, "radius": 0.89 * mm});
            skArc(sketch, "E20.0", {"start": v(-78.36, 0) * mm, "mid": v(-79.88, 3.38) * mm, "end": v(-76.34, 2.29) * mm});
            skCircle(sketch, "E21", {"center": v(-78.36, 2.03) * mm, "radius": 2.03 * mm});
            skLineSegment(sketch, "E22", {"start": v(-76.34, 2.29) * mm, "end": v(-76.2, 2.29) * mm});
            skLineSegment(sketch, "E23", {"start": v(-76.2, 2.29) * mm, "end": v(-76.2, 0) * mm});
            skLineSegment(sketch, "E24", {"start": v(-76.2, 0) * mm, "end": v(-78.36, 0) * mm});
            skSolve(sketch);
        }
        {
            var Q0;
            Q0=qSketchRegion(id+"F14",true);
            extrude(context, id + "F15", {"entities" : qUnion([Q0]), "operationType" : NewBodyOperationType.ADD, "oppositeDirection" : true, "depth" : 7.62 * mm, "offsetDistance" : 25.4 * mm});
        }
        {
            var Q0;
            Q0=qCreatedBy(makeId("Top.planeOp"),FACE);
            var sketch = newSketch(context, id + "F16", { "sketchPlane" : qUnion([Q0])});
            skLineSegment(sketch, "E25.bottom", {"start": v(89.03, 33.27) * mm, "end": v(109.35, 33.27) * mm});
            skLineSegment(sketch, "E25.top", {"start": v(89.03, 28.2) * mm, "end": v(109.35, 28.2) * mm});
            skLineSegment(sketch, "E25.left", {"start": v(89.03, 33.27) * mm, "end": v(89.03, 28.2) * mm});
            skLineSegment(sketch, "E25.right", {"start": v(109.35, 33.27) * mm, "end": v(109.35, 28.2) * mm});
            skPoint(sketch, "E25.middle", {"position": v(99.19, 30.73) * mm});
            skLineSegment(sketch, "E26.0", {"start": v(86.74, 35.56) * mm, "end": v(111.63, 35.56) * mm});
            skLineSegment(sketch, "E26.1", {"start": v(86.74, 35.56) * mm, "end": v(86.74, 25.9) * mm});
            skLineSegment(sketch, "E26.2", {"start": v(86.74, 25.9) * mm, "end": v(111.63, 25.9) * mm});
            skLineSegment(sketch, "E26.3", {"start": v(111.63, 35.56) * mm, "end": v(111.63, 25.9) * mm});
            skLineSegment(sketch, "E27.0", {"start": v(80.4, 25.9) * mm, "end": v(76.34, 25.9) * mm});
            skSolve(sketch);
        }
        {
            var Q0;
            Q0=qSketchRegion(id+"F16",true);
            extrude(context, id + "F17", {"entities" : qUnion([Q0]), "depth" : 10.16 * mm, "offsetDistance" : 25.4 * mm});
        }
        {
            var Q0;
            Q0=makeQuery(id+"F15.boolean.opBoolean","MERGE",FACE,{"derivedFrom":[makeQuery(id+"F13.boolean.opBoolean","MERGE",FACE,{"derivedFrom":[makeQuery(id+"F8.opExtrude","CAP_FACE",FACE,{"disambiguationData":[OSD([sQuery(id+"F7.wireOp",EDGE,"E12.bottom"),sQuery(id+"F7.wireOp",EDGE,"E12.top"),sQuery(id+"F7.wireOp",EDGE,"E12.left"),sQuery(id+"F7.wireOp",EDGE,"E12.right")])],"isStart":true}),makeQuery(id+"F13.opExtrude","SWEPT_FACE",FACE,{"disambiguationData":[OSD([sQuery(id+"F12.wireOp",EDGE,"E17")])]})]}),makeQuery(id+"F15.opExtrude","SWEPT_FACE",FACE,{"disambiguationData":[OSD([sQuery(id+"F14.wireOp",EDGE,"E24")])]})]});
            var sketch = newSketch(context, id + "F18", { "sketchPlane" : qUnion([Q0])});
            skLineSegment(sketch, "E28.bottom", {"start": v(-0.76, -27.69) * mm, "end": v(0.76, -27.69) * mm});
            skLineSegment(sketch, "E28.top", {"start": v(-0.76, -31.5) * mm, "end": v(0.76, -31.5) * mm});
            skLineSegment(sketch, "E28.left", {"start": v(-0.76, -27.69) * mm, "end": v(-0.76, -31.5) * mm});
            skLineSegment(sketch, "E28.right", {"start": v(0.76, -27.69) * mm, "end": v(0.76, -31.5) * mm});
            skPoint(sketch, "E28.middle", {"position": v(0, -29.6) * mm});
            skSolve(sketch);
        }
        {
            var Q0;
            Q0=qSketchRegion(id+"F18",true);
            extrude(context, id + "F19", {"entities" : qUnion([Q0]), "operationType" : NewBodyOperationType.REMOVE, "endBound" : BoundingType.UP_TO_NEXT, "oppositeDirection" : true, "depth" : 25.4 * mm, "offsetDistance" : 25.4 * mm});
        }
        {
            var Q0;
            Q0=makeQuery(id+"F13.boolean.opBoolean","MERGE",EDGE,{"derivedFrom":[makeQuery(id+"F8.opExtrude","CAP_EDGE",EDGE,{"disambiguationData":[OSD([sQuery(id+"F7.wireOp",EDGE,"E12.bottom")])],"isStart":false}),makeQuery(id+"F13.opExtrude","CAP_EDGE",EDGE,{"disambiguationData":[OSD([sQuery(id+"F12.wireOp",EDGE,"E18")])],"isStart":true})]});
            var Q1;
            Q1=makeQuery(id+"F13.boolean.opBoolean","MERGE",EDGE,{"derivedFrom":[makeQuery(id+"F8.opExtrude","CAP_EDGE",EDGE,{"disambiguationData":[OSD([sQuery(id+"F7.wireOp",EDGE,"E12.bottom")])],"isStart":true}),makeQuery(id+"F13.opExtrude","CAP_EDGE",EDGE,{"disambiguationData":[OSD([sQuery(id+"F12.wireOp",EDGE,"E17")])],"isStart":true})]});
            var Q2;
            Q2=makeQuery(id+"F15.boolean.opBoolean","MERGE",EDGE,{"derivedFrom":[makeQuery(id+"F8.opExtrude","CAP_EDGE",EDGE,{"disambiguationData":[OSD([sQuery(id+"F7.wireOp",EDGE,"E12.top")])],"isStart":false}),makeQuery(id+"F15.opExtrude","CAP_EDGE",EDGE,{"disambiguationData":[OSD([sQuery(id+"F14.wireOp",EDGE,"E22")])],"isStart":true})]});
            var Q3;
            Q3=makeQuery(id+"F15.boolean.opBoolean","MERGE",EDGE,{"derivedFrom":[makeQuery(id+"F8.opExtrude","CAP_EDGE",EDGE,{"disambiguationData":[OSD([sQuery(id+"F7.wireOp",EDGE,"E12.top")])],"isStart":true}),makeQuery(id+"F15.opExtrude","CAP_EDGE",EDGE,{"disambiguationData":[OSD([sQuery(id+"F14.wireOp",EDGE,"E24")])],"isStart":true})]});
            var Q4;
            Q4=makeQuery(id+"F1.opExtrude","CAP_EDGE",EDGE,{"disambiguationData":[OSD([sQuery(id+"F0.wireOp",EDGE,"E0.bottom")])],"isStart":true});
            var Q5;
            Q5=makeQuery(id+"F1.opExtrude","CAP_EDGE",EDGE,{"disambiguationData":[OSD([sQuery(id+"F0.wireOp",EDGE,"E0.bottom")])],"isStart":false});
            var Q6;
            Q6=makeQuery(id+"F17.opExtrude","CAP_EDGE",EDGE,{"disambiguationData":[OSD([sQuery(id+"F16.wireOp",EDGE,"E26.2")])],"isStart":true});
            var Q7;
            Q7=makeQuery(id+"F17.opExtrude","CAP_EDGE",EDGE,{"disambiguationData":[OSD([sQuery(id+"F16.wireOp",EDGE,"E26.3")])],"isStart":true});
            var Q8;
            Q8=makeQuery(id+"F17.opExtrude","CAP_EDGE",EDGE,{"disambiguationData":[OSD([sQuery(id+"F16.wireOp",EDGE,"E26.0")])],"isStart":true});
            var Q9;
            Q9=makeQuery(id+"F17.opExtrude","CAP_EDGE",EDGE,{"disambiguationData":[OSD([sQuery(id+"F16.wireOp",EDGE,"E26.1")])],"isStart":true});
            var Q10;
            Q10=makeQuery(id+"F17.opExtrude","CAP_EDGE",EDGE,{"disambiguationData":[OSD([sQuery(id+"F16.wireOp",EDGE,"E26.1")])],"isStart":false});
            var Q11;
            Q11=makeQuery(id+"F17.opExtrude","CAP_EDGE",EDGE,{"disambiguationData":[OSD([sQuery(id+"F16.wireOp",EDGE,"E26.0")])],"isStart":false});
            var Q12;
            Q12=makeQuery(id+"F17.opExtrude","CAP_EDGE",EDGE,{"disambiguationData":[OSD([sQuery(id+"F16.wireOp",EDGE,"E26.2")])],"isStart":false});
            var Q13;
            Q13=makeQuery(id+"F17.opExtrude","CAP_EDGE",EDGE,{"disambiguationData":[OSD([sQuery(id+"F16.wireOp",EDGE,"E26.3")])],"isStart":false});
            var Q14;
            Q14=makeQuery(id+"F8.opExtrude","CAP_EDGE",EDGE,{"disambiguationData":[OSD([sQuery(id+"F7.wireOp",EDGE,"E12.right")])],"isStart":true});
            var Q15;
            Q15=makeQuery(id+"F8.opExtrude","CAP_EDGE",EDGE,{"disambiguationData":[OSD([sQuery(id+"F7.wireOp",EDGE,"E12.right")])],"isStart":false});
            var Q16;
            Q16=makeQuery(id+"F17.opExtrude","SWEPT_EDGE",EDGE,{"disambiguationData":[OSD([sQuery(id+"F16.wireOp",EDGE,"E26.0"),sQuery(id+"F16.wireOp",EDGE,"E26.3")])]});
            var Q17;
            Q17=makeQuery(id+"F17.opExtrude","SWEPT_EDGE",EDGE,{"disambiguationData":[OSD([sQuery(id+"F16.wireOp",EDGE,"E26.0"),sQuery(id+"F16.wireOp",EDGE,"E26.1")])]});
            var Q18;
            Q18=makeQuery(id+"F17.opExtrude","SWEPT_EDGE",EDGE,{"disambiguationData":[OSD([sQuery(id+"F16.wireOp",EDGE,"E26.2"),sQuery(id+"F16.wireOp",EDGE,"E26.3")])]});
            var Q19;
            Q19=makeQuery(id+"F17.opExtrude","SWEPT_EDGE",EDGE,{"disambiguationData":[OSD([sQuery(id+"F16.wireOp",EDGE,"E26.1"),sQuery(id+"F16.wireOp",EDGE,"E26.2")])]});
            fillet(context, id + "F20", {"entities" : qUnion([Q0, Q1, Q2, Q3, Q4, Q5, Q6, Q7, Q8, Q9, Q10, Q11, Q12, Q13, Q14, Q15, Q16, Q17, Q18, Q19]), "radius" : 1.14 * mm, "tangentPropagation" : true, "allowEdgeOverflow" : false});
        }
        {
            var Q0;
            Q0=makeQuery(id+"F17.opExtrude","SWEPT_BODY",BODY,{"disambiguationData":[OSD([sQuery(id+"F16.wireOp",EDGE,"E25.bottom"),sQuery(id+"F16.wireOp",EDGE,"E25.top"),sQuery(id+"F16.wireOp",EDGE,"E25.left"),sQuery(id+"F16.wireOp",EDGE,"E25.right"),sQuery(id+"F16.wireOp",EDGE,"E26.0"),sQuery(id+"F16.wireOp",EDGE,"E26.1"),sQuery(id+"F16.wireOp",EDGE,"E26.2"),sQuery(id+"F16.wireOp",EDGE,"E26.3")])]});
            deleteBodies(context, id + "F21", {"entities" : qUnion([Q0])});
        }
        {
            var Q0;
            Q0=makeQuery(id+"F8.opExtrude","SWEPT_BODY",BODY,{"disambiguationData":[OSD([sQuery(id+"F7.wireOp",EDGE,"E12.bottom"),sQuery(id+"F7.wireOp",EDGE,"E12.top"),sQuery(id+"F7.wireOp",EDGE,"E12.left"),sQuery(id+"F7.wireOp",EDGE,"E12.right")])]});
            deleteBodies(context, id + "F22", {"entities" : qUnion([Q0])});
        }
    });
